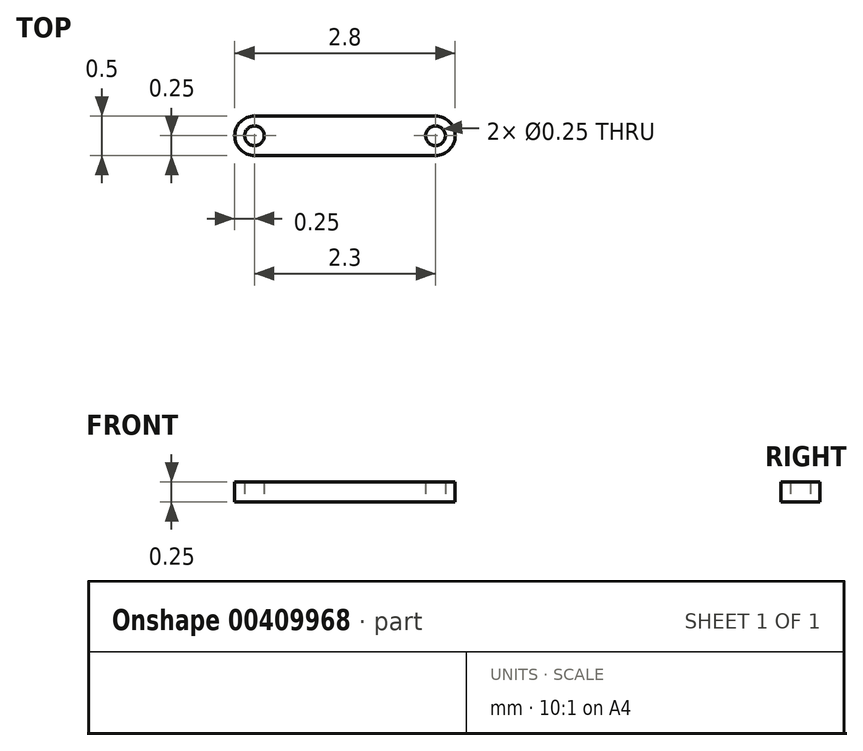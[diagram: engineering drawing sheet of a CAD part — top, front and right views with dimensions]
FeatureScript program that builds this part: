
annotation { "Feature Type Name" : "Feature", "Feature Type Description" : "" }
export const myFeature = defineFeature(function(context is Context, id is Id, definition is map)
    precondition{}
    {
        {
            var Q0;
            Q0=qCreatedBy(makeId("Top.planeOp"),FACE);
            var sketch = newSketch(context, id + "F0", { "sketchPlane" : qUnion([Q0])});
            skLineSegment(sketch, "E0.bottom", {"start": v(-2.3, 0.25) * mm, "end": v(0, 0.25) * mm});
            skLineSegment(sketch, "E0.top", {"start": v(-2.3, -0.25) * mm, "end": v(0, -0.25) * mm});
            skLineSegment(sketch, "E0.left", {"start": v(-2.55, 0) * mm, "end": v(-2.55, 0) * mm});
            skLineSegment(sketch, "E0.right", {"start": v(0.25, 0) * mm, "end": v(0.25, 0) * mm});
            skLineSegment(sketch, "E1", {"start": v(0, -9.02) * mm, "end": v(0, 8.79) * mm, "construction": true});
            skPoint(sketch, "E2.visualSharp", {"position": v(-2.55, 0.25) * mm});
            skArc(sketch, "E2.filletArc", {"start": v(-2.3, 0.25) * mm, "mid": v(-2.48, 0.18) * mm, "end": v(-2.55, 0) * mm});
            skPoint(sketch, "E3.visualSharp", {"position": v(-2.55, -0.25) * mm});
            skArc(sketch, "E3.filletArc", {"start": v(-2.55, 0) * mm, "mid": v(-2.48, -0.18) * mm, "end": v(-2.3, -0.25) * mm});
            skPoint(sketch, "E4.visualSharp", {"position": v(0.25, 0.25) * mm});
            skArc(sketch, "E4.filletArc", {"start": v(0.25, 0) * mm, "mid": v(0.18, 0.18) * mm, "end": v(0, 0.25) * mm});
            skPoint(sketch, "E5.visualSharp", {"position": v(0.25, -0.25) * mm});
            skArc(sketch, "E5.filletArc", {"start": v(0, -0.25) * mm, "mid": v(0.18, -0.18) * mm, "end": v(0.25, 0) * mm});
            skCircle(sketch, "E6", {"center": v(-2.3, 0) * mm, "radius": 0.12 * mm});
            skCircle(sketch, "E7", {"center": v(0, 0) * mm, "radius": 0.12 * mm});
            skSolve(sketch);
        }
        {
            var Q0;
            Q0 = qSketchRegion(id + "F0", true);
            extrude(context, id + "F1", {"entities" : qUnion([Q0]), "depth" : 0.25 * mm});
        }
    });
